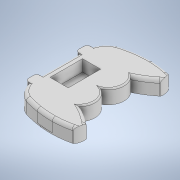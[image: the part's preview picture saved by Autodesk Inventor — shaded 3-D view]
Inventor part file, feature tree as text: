
AUTODESK INVENTOR PART (.ipt)
format: ipt  version: 2022 (Build 260153000, 153)  size: 494,080 bytes
history: native  units: mm
features: sketch x6, extrude x5, fillet x2
ambient origin geometry x8: Origin, YZ Plane, XZ Plane, XY Plane, X Axis, Y Axis, Z Axis, Center Point
bodies: Solid1 (feature_tree)
feature tree (13):
  sketch  "Sketch1"  dims[d0=35.0mm d1=60.0mm]
  extrude  "Extrusion1"  Depth=60.0mm
  extrude  "Extrusion2"  Depth=25.0mm
  fillet  "Fillet1"  Radius=22.5mm
  extrude  "Extrusion3"  Depth=25.0mm
  fillet  "Fillet2"  Radius=34.0mm
  extrude  "Extrusion4"  Depth=7.5mm
  extrude  "Extrusion5"  Depth=25.0mm
  sketch  "Sketch2"  dims[d2=17.5mm d3=25.0mm d4=22.5mm]
  sketch  "Sketch4"  dims[d6=25.0mm d7=27.0mm d8=34.0mm]
  sketch  "Sketch5"  dims[d9=27.0mm d10=7.5mm]
  sketch  "Sketch6"  dims[d11=25.0mm d12=27.0mm d13=34.0mm d14=27.0mm]
  sketch  "Sketch7"  dims[d15=6.0mm d16=6.0mm d17=6.0mm d18=6.5mm d22=6.0mm d23=40.0mm d25=360.0deg d27=25.0mm d28=27.0mm d31=40.0mm d32=25.0mm d33=27.0mm d34=5.0mm d35=8.0mm d36=8.0mm d58=40.0mm d60=360.0deg d62=50.0mm d63=2.0mm d64=0.0mm d70=13.425896mm d72=37.3mm d73=4.0mm d74=37.3mm d86=6.5mm d93=0.5mm d95=40.0mm d97=40.0mm d98=20.0mm d99=0.0mm d100=5.0mm d101=10.0mm d102=0.0mm d103=2.0mm d104=25.0mm d105=28.0mm d106=50.0mm d107=10.0mm d108=15.0mm d109=0.0mm d110=2.0mm d111=0.0mm d112=4.0mm d113=4.0mm]
